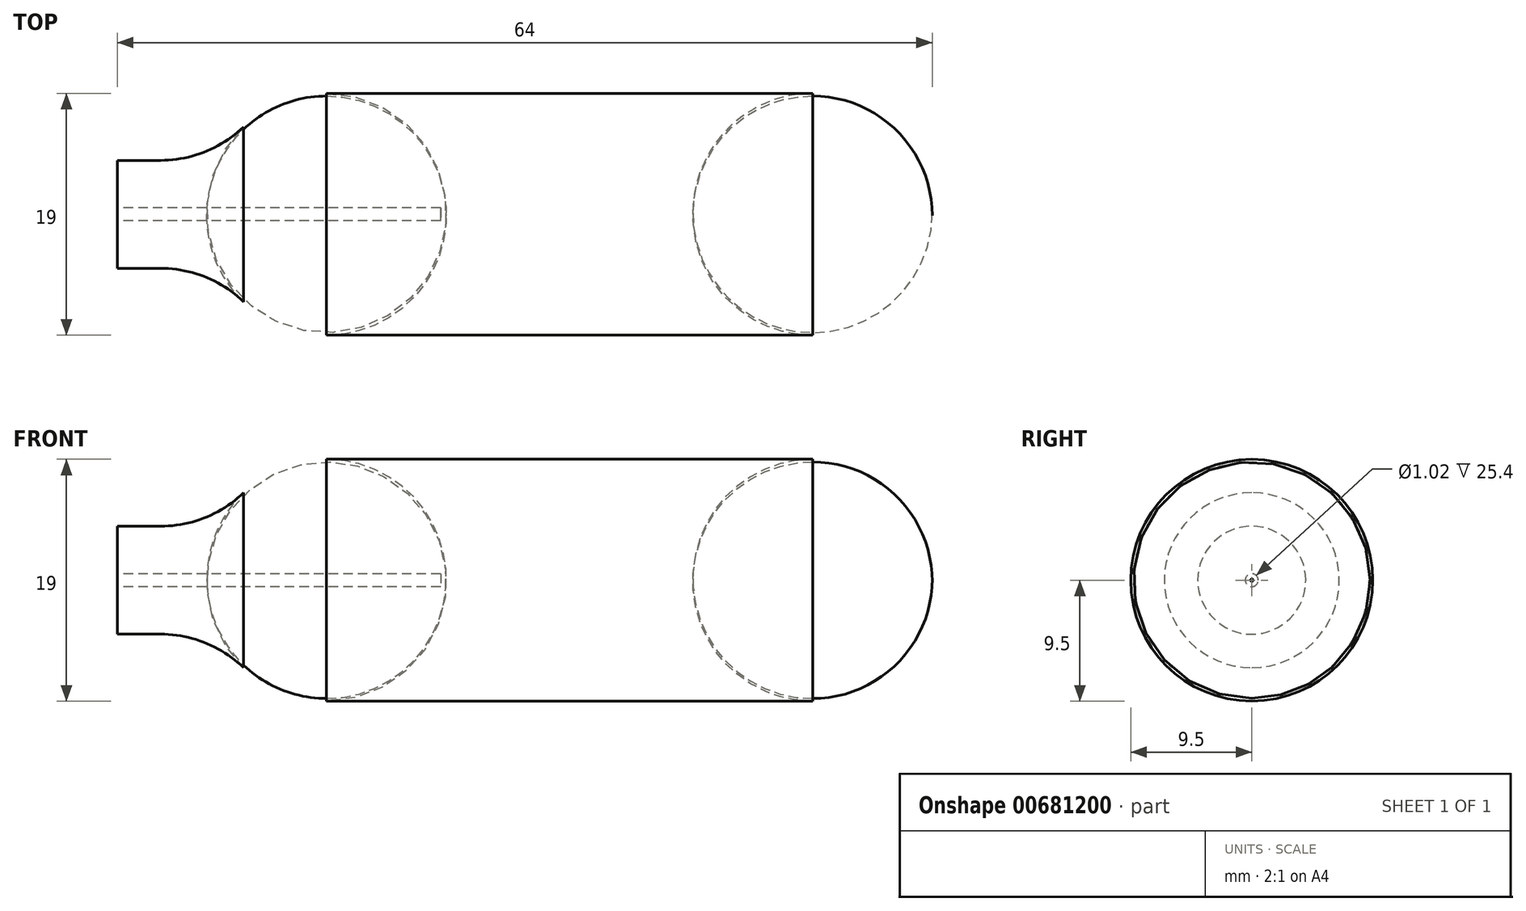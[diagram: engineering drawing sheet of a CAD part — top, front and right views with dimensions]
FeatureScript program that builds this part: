
annotation { "Feature Type Name" : "Feature", "Feature Type Description" : "" }
export const myFeature = defineFeature(function(context is Context, id is Id, definition is map)
    precondition{}
    {
        {
            var Q0;
            Q0=qCreatedBy(makeId("Front.planeOp"),FACE);
            var sketch = newSketch(context, id + "F0", { "sketchPlane" : qUnion([Q0])});
            skLineSegment(sketch, "E0", {"start": v(0, 0) * mm, "end": v(32.5, 0) * mm});
            skLineSegment(sketch, "E1", {"start": v(32.5, 0) * mm, "end": v(32.5, 9.5) * mm});
            skLineSegment(sketch, "E2", {"start": v(32.5, 9.5) * mm, "end": v(-23.51, 9.5) * mm});
            skLineSegment(sketch, "E3", {"start": v(-23.51, 9.5) * mm, "end": v(-23.51, 4.24) * mm});
            skLineSegment(sketch, "E4", {"start": v(-23.51, 4.24) * mm, "end": v(-31.51, 4.24) * mm});
            skLineSegment(sketch, "E5", {"start": v(-31.51, 4.24) * mm, "end": v(-31.51, 0) * mm});
            skLineSegment(sketch, "E6", {"start": v(-31.51, 0) * mm, "end": v(0, 0) * mm});
            skSolve(sketch);
        }
        {
            var Q0;
            Q0=makeQuery(id+"F0.imprint","IMPRINT",FACE,{"disambiguationData":[TD([[makeQuery(id+"F0.imprint","IMPRINT",EDGE,{"derivedFrom":sQuery(id+"F0.wireOp",EDGE,"E0")}),1.0]])]});
            var Q1;
            Q1=sQuery(id+"F0.wireOp",EDGE,"E0");
            revolve(context, id + "F1", {"entities" : qUnion([Q0]), "axis" : qUnion([Q1]), "revolveType" : RevolveType.FULL});
        }
        {
            var Q0;
            Q0=makeQuery(id+"F1.opRevolve","SWEPT_FACE",FACE,{"disambiguationData":[OSD([sQuery(id+"F0.wireOp",EDGE,"E1")])]});
            fillet(context, id + "F2", {"entities" : qUnion([Q0]), "radius" : 9.4 * mm, "tangentPropagation" : true, "allowEdgeOverflow" : false});
        }
        {
            var Q0;
            Q0=makeQuery(id+"F1.opRevolve","SWEPT_EDGE",EDGE,{"disambiguationData":[OSD([sQuery(id+"F0.wireOp",EDGE,"E2"),sQuery(id+"F0.wireOp",EDGE,"E3")])]});
            fillet(context, id + "F3", {"entities" : qUnion([Q0]), "radius" : 9.4 * mm, "tangentPropagation" : true, "allowEdgeOverflow" : false});
        }
        {
            var Q0;
            Q0=makeQuery(id+"F3.opFillet","BLEND_EDGE",EDGE,{"blendedFrom":[makeQuery(id+"F1.opRevolve","SWEPT_EDGE",EDGE,{"disambiguationData":[OSD([sQuery(id+"F0.wireOp",EDGE,"E2"),sQuery(id+"F0.wireOp",EDGE,"E3")])]}),makeQuery(id+"F1.opRevolve","SWEPT_FACE",FACE,{"disambiguationData":[OSD([sQuery(id+"F0.wireOp",EDGE,"E4")])]})],"blendedInto":[makeQuery(id+"F1.opRevolve","SWEPT_FACE",FACE,{"disambiguationData":[OSD([sQuery(id+"F0.wireOp",EDGE,"E4")])]})]});
            fillet(context, id + "F4", {"entities" : qUnion([Q0]), "radius" : 9.4 * mm, "tangentPropagation" : true, "allowEdgeOverflow" : false});
        }
        {
            var Q0;
            Q0=makeQuery(id+"F1.opRevolve","SWEPT_FACE",FACE,{"disambiguationData":[OSD([sQuery(id+"F0.wireOp",EDGE,"E5")])]});
            var sketch = newSketch(context, id + "F5", { "sketchPlane" : qUnion([Q0])});
            skCircle(sketch, "E7", {"center": v(0, 0) * mm, "radius": 0.5 * mm});
            skSolve(sketch);
        }
        {
            var Q0;
            Q0=makeQuery(id+"F5.imprint","IMPRINT",FACE,{"disambiguationData":[TD([[makeQuery(id+"F5.imprint","IMPRINT",EDGE,{"derivedFrom":sQuery(id+"F5.wireOp",EDGE,"E7")}),1.0]])]});
            extrude(context, id + "F6", {"entities" : qUnion([Q0]), "operationType" : NewBodyOperationType.REMOVE, "oppositeDirection" : true, "depth" : 25.4 * mm, "offsetDistance" : 25.4 * mm});
        }
    });
